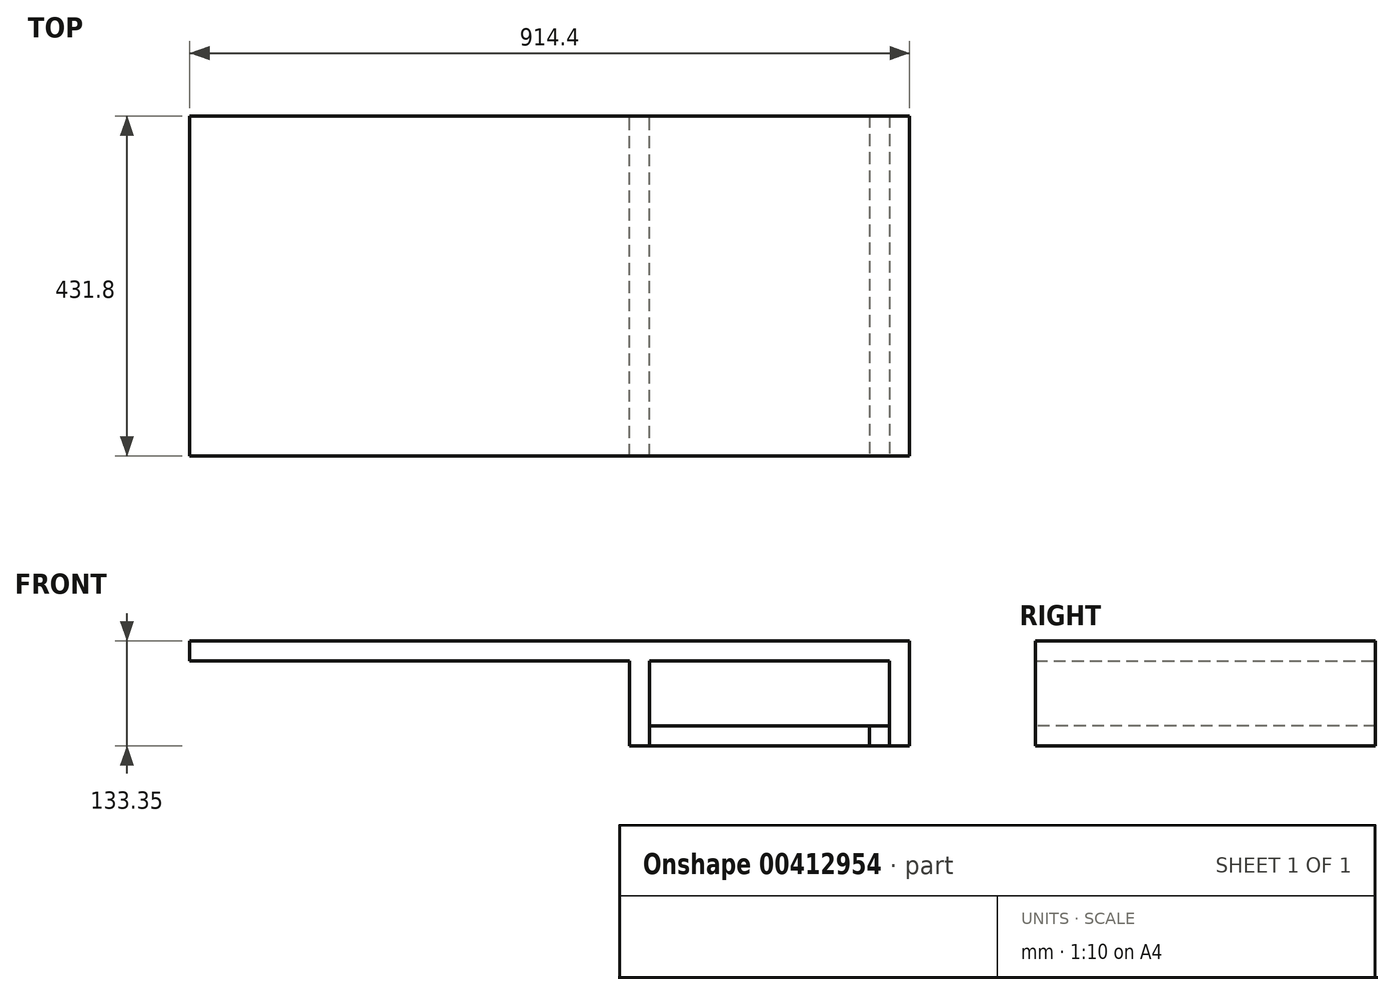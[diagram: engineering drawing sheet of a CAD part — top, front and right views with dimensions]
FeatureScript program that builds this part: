
annotation { "Feature Type Name" : "Feature", "Feature Type Description" : "" }
export const myFeature = defineFeature(function(context is Context, id is Id, definition is map)
    precondition{}
    {
        {
            var Q0;
            Q0=qCreatedBy(makeId("Top.planeOp"),FACE);
            var sketch = newSketch(context, id + "F0", { "sketchPlane" : qUnion([Q0])});
            skLineSegment(sketch, "E0.bottom", {"start": v(-423.64, 242.5) * mm, "end": v(490.76, 242.5) * mm});
            skLineSegment(sketch, "E0.top", {"start": v(-423.64, -189.3) * mm, "end": v(490.76, -189.3) * mm});
            skLineSegment(sketch, "E0.left", {"start": v(-423.64, 242.5) * mm, "end": v(-423.64, -189.3) * mm});
            skLineSegment(sketch, "E0.right", {"start": v(490.76, 242.5) * mm, "end": v(490.76, -189.3) * mm});
            skSolve(sketch);
        }
        {
            var Q0;
            Q0 = qSketchRegion(id + "F0", true);
            extrude(context, id + "F1", {"entities" : qUnion([Q0]), "depth" : 25.4 * mm});
        }
        {
            var Q0;
            Q0=makeQuery(id+"F1.opExtrude","CAP_FACE",FACE,{"disambiguationData":[OSD([sQuery(id+"F0.wireOp",EDGE,"E0.bottom"),sQuery(id+"F0.wireOp",EDGE,"E0.top"),sQuery(id+"F0.wireOp",EDGE,"E0.left"),sQuery(id+"F0.wireOp",EDGE,"E0.right")])],"isStart":true});
            var sketch = newSketch(context, id + "F2", { "sketchPlane" : qUnion([Q0])});
            skLineSegment(sketch, "E1.bottom", {"start": v(490.76, 189.3) * mm, "end": v(465.36, 189.3) * mm});
            skLineSegment(sketch, "E1.top", {"start": v(490.76, -242.5) * mm, "end": v(465.36, -242.5) * mm});
            skLineSegment(sketch, "E1.left", {"start": v(490.76, 189.3) * mm, "end": v(490.76, -242.5) * mm});
            skLineSegment(sketch, "E1.right", {"start": v(465.36, 189.3) * mm, "end": v(465.36, -242.5) * mm});
            skLineSegment(sketch, "E2.bottom", {"start": v(160.56, 189.3) * mm, "end": v(135.16, 189.3) * mm});
            skLineSegment(sketch, "E2.top", {"start": v(160.56, -242.5) * mm, "end": v(135.16, -242.5) * mm});
            skLineSegment(sketch, "E2.left", {"start": v(160.56, 189.3) * mm, "end": v(160.56, -242.5) * mm});
            skLineSegment(sketch, "E2.right", {"start": v(135.16, 189.3) * mm, "end": v(135.16, -242.5) * mm});
            skSolve(sketch);
        }
        {
            var Q0;
            Q0 = qSketchRegion(id + "F2", true);
            extrude(context, id + "F3", {"entities" : qUnion([Q0]), "operationType" : NewBodyOperationType.ADD, "depth" : 107.95 * mm});
        }
        {
            var Q0;
            Q0=makeQuery(id+"F3.opExtrude","SWEPT_FACE",FACE,{"disambiguationData":[OSD([sQuery(id+"F2.wireOp",EDGE,"E1.right")])]});
            var sketch = newSketch(context, id + "F4", { "sketchPlane" : qUnion([Q0])});
            skLineSegment(sketch, "E3.bottom", {"start": v(-242.5, -107.95) * mm, "end": v(189.3, -107.95) * mm});
            skLineSegment(sketch, "E3.top", {"start": v(-242.5, -82.55) * mm, "end": v(189.3, -82.55) * mm});
            skLineSegment(sketch, "E3.left", {"start": v(-242.5, -107.95) * mm, "end": v(-242.5, -82.55) * mm});
            skLineSegment(sketch, "E3.right", {"start": v(189.3, -107.95) * mm, "end": v(189.3, -82.55) * mm});
            skSolve(sketch);
        }
        {
            var Q0;
            Q0 = qSketchRegion(id + "F4", true);
            extrude(context, id + "F5", {"entities" : qUnion([Q0]), "depth" : 25.4 * mm});
        }
        {
            var Q0;
            Q0 = qSketchRegion(id + "F4", true);
            extrude(context, id + "F6", {"entities" : qUnion([Q0]), "depth" : 304.8 * mm});
        }
    });
